# Revit family: Faucet-Handle-KOHLER-ARTIFACTS-98068W
name_source: partatom
category: Plumbing Fixtures
revit_build: Autodesk Revit 2017 (Build: 20160225_1515(x64)
units: mm (PartAtom-declared; Revit-internal decimal feet)

## family parameters
Cut with Voids When Loaded = No
Host = Face
OmniClass Number = 23.31.11.00
OmniClass Title = Faucets
Part Type = Normal
Room Calculation Point = No
Round Connector Dimension = Use Diameter
Shared = No

## types (3) — shared parameters
ADA Compliant = No
Assembly Code = D2010
CW Connection = Yes
Cold Water Inlet = Cold Water Inlet
Date Modified = 08/27/2020
Default Elevation = 36"
Drain Included = Yes
Finish = Kohler-Metal-CP-Polished_Chrome
Flow Rate = 0 GPM
HW Connection = Yes
Hot Water Inlet = Hot Water Inlet
Length = 2 1/4"
Manufacturer = KOHLER Co.
Master Format 2014 = 22 41 39
Master Format 2014 Name = Residential Faucets, Supplies, and Trim
Material = Metal construction
Pressure = 0.00 psi
Product Documentation Link = https://resources.kohler.com
Product Name = ARTIFACTS
Product Page URL = https://www.kohler.co.uk
URL = https://www.kohler.co.uk
Vent Connection = No
Waste Connection = No
Waste Water Outlet = Waste Water Outlet
WaterSense Certified = No

## per-type parameters (varying)
| type | Description | Model | TF | Type | _3M | _4 | _9M |
| Prong Handle, CP-Polished chrome | Prong Handles | 98068W-3M-CP | 5" | 1 | Yes | No | No |
| Lever Handle, CP-Polished Chrome | Lever Handles | 98068W-4-CP | 0" | 2 | No | Yes | No |
| Swing lever Handle, CP- Polished chrome | Swing Lever Handles | 98068W-9M-CP | 10" | 3 | No | No | Yes |

## geometry (parser evidence)
native form markers: Sweep x7
no freeform markers — native parametric forms only
